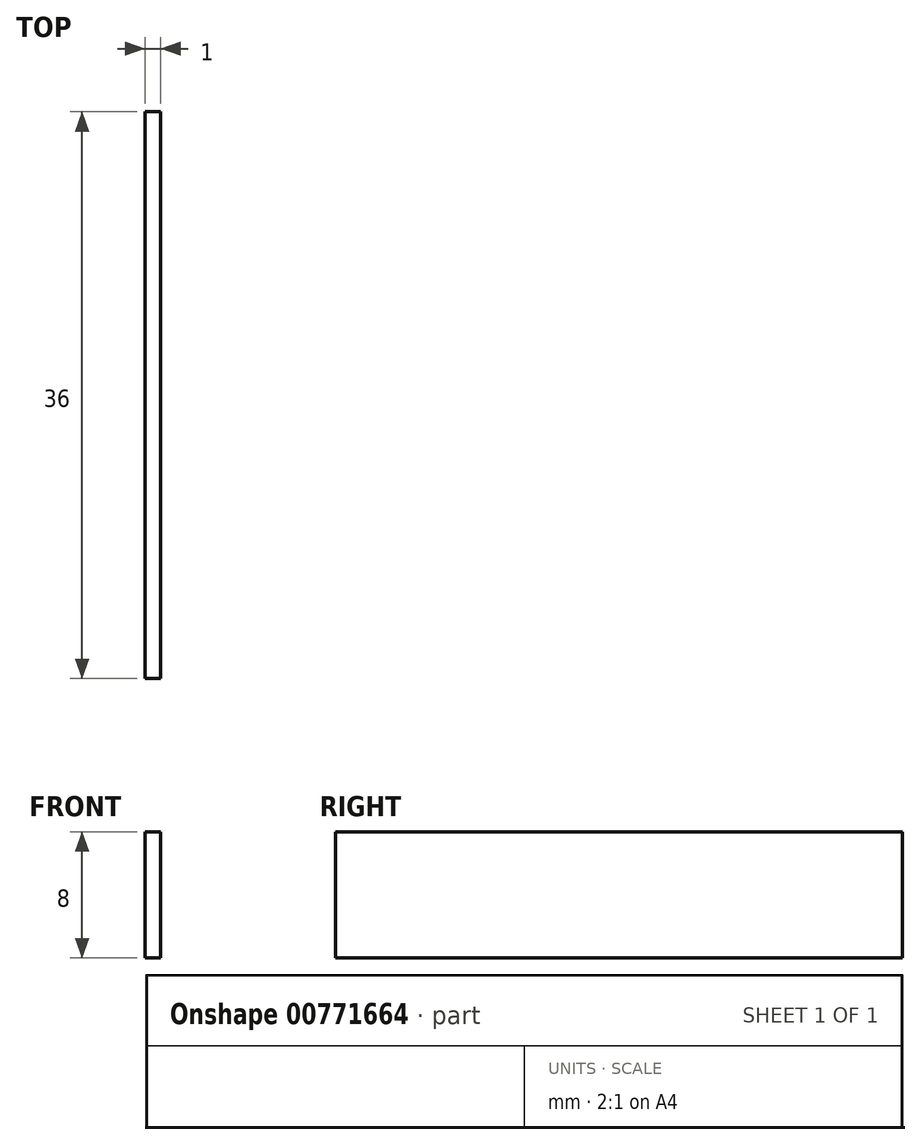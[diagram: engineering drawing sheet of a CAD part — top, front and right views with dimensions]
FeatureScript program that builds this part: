
annotation { "Feature Type Name" : "Feature", "Feature Type Description" : "" }
export const myFeature = defineFeature(function(context is Context, id is Id, definition is map)
    precondition{}
    {
        {
            var Q0;
            Q0=qCreatedBy(makeId("Top.planeOp"),FACE);
            var sketch = newSketch(context, id + "F0", { "sketchPlane" : qUnion([Q0])});
            skLineSegment(sketch, "E0.bottom", {"start": v(-31.68, 18.43) * mm, "end": v(-30.68, 18.43) * mm});
            skLineSegment(sketch, "E0.top", {"start": v(-31.68, -17.57) * mm, "end": v(-30.68, -17.57) * mm});
            skLineSegment(sketch, "E0.left", {"start": v(-31.68, 18.43) * mm, "end": v(-31.68, -17.57) * mm});
            skLineSegment(sketch, "E0.right", {"start": v(-30.68, 18.43) * mm, "end": v(-30.68, -17.57) * mm});
            skSolve(sketch);
        }
        {
            var Q0;
            Q0=qSketchRegion(id+"F0",true);
            extrude(context, id + "F1", {"entities" : qUnion([Q0]), "depth" : 8 * mm, "offsetDistance" : 25 * mm});
        }
    });
